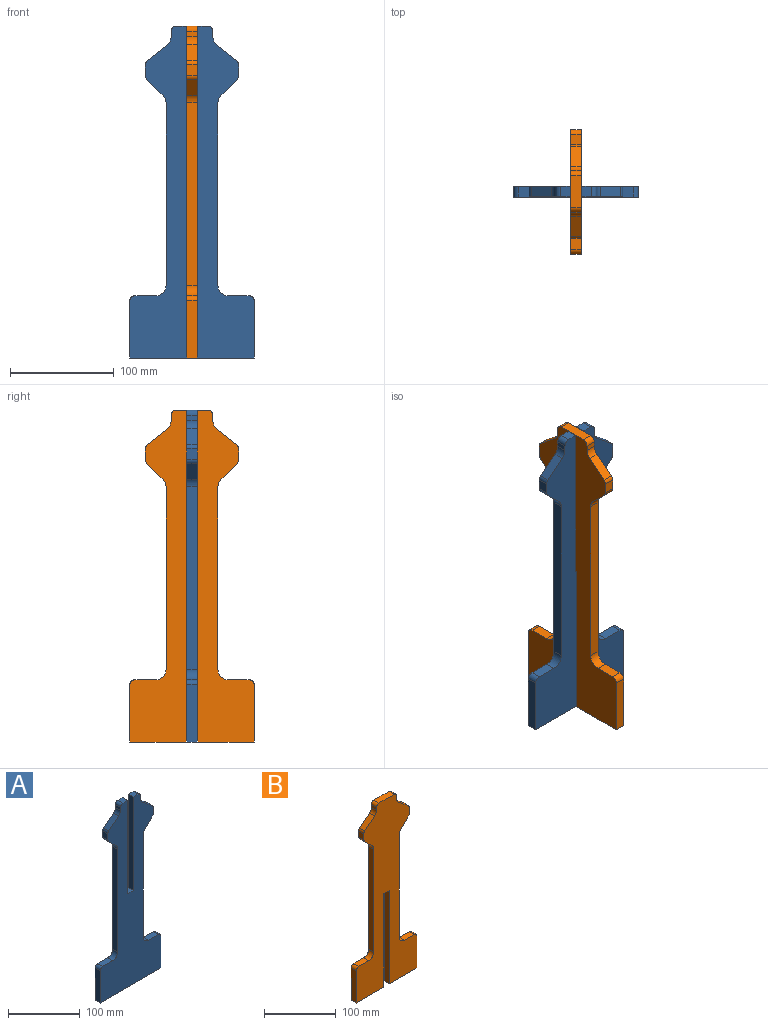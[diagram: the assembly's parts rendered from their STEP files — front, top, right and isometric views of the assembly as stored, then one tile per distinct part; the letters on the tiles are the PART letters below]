
ASSEMBLY  parts=2 mates=1
PART A: 36 faces, bbox 120x10x320 mm
  f0: plane 120x10mm, normal (0,0,-1), area 1200mm2, adj f1,f33,f34,f35
  f1: plane 55x10mm, normal (1,0,0), area 550mm2, adj f0,f2,f34,f35
  f2: cylinder r=5mm len=10mm, axis (0,-1,0), area 78.5mm2, adj f1,f3,f34,f35
  f3: plane 20x10mm, normal (0,0,1), area 200mm2, adj f2,f4,f34,f35
  f4: cylinder r=10mm len=10mm, axis (0,-1,0), area 157.1mm2, adj f3,f5,f34,f35
  f5: plane 175.86x10mm, normal (1,0,0), area 1758.6mm2, adj f4,f6,f34,f35
  f6: cylinder r=10mm len=10mm, axis (0,-1,0), area 78.5mm2, adj f5,f7,f34,f35
  f7: plane 15.61x15.61mm, normal (0.71,0,-0.71), area 220.7mm2, adj f6,f8,f34,f35
  f8: cylinder r=5mm len=10mm, axis (0,-1,0), area 39.3mm2, adj f7,f9,f34,f35
  f9: plane 10.53x10mm, normal (1,0,0), area 105.3mm2, adj f8,f10,f34,f35
  f10: cylinder r=5mm len=10mm, axis (0,-1,0), area 44.8mm2, adj f9,f11,f34,f35
  f11: plane 19.37x15.5mm, normal (0.62,0,0.78), area 248.1mm2, adj f10,f12,f34,f35
  f12: cylinder r=10mm len=10mm, axis (0,-1,0), area 89.6mm2, adj f11,f13,f34,f35
  f13: plane 10x5.19mm, normal (1,0,0), area 51.9mm2, adj f12,f14,f34,f35
  f14: cylinder r=5mm len=10mm, axis (0,-1,0), area 78.5mm2, adj f13,f15,f34,f35
  f15: plane 10x9.5mm, normal (0,0,1), area 95mm2, adj f14,f16,f34,f35
  f16: plane 160x10mm, normal (-1,0,0), area 1600mm2, adj f15,f17,f34,f35
  f17: plane 11x10mm, normal (0,0,1), area 110mm2, adj f16,f18,f34,f35
  f18: plane 160x10mm, normal (1,0,0), area 1600mm2, adj f17,f19,f34,f35
  f19: plane 10x9.5mm, normal (0,0,1), area 95mm2, adj f18,f20,f34,f35
  f20: cylinder r=5mm len=10mm, axis (0,-1,0), area 78.5mm2, adj f19,f21,f34,f35
  f21: plane 10x5.19mm, normal (-1,0,0), area 51.9mm2, adj f20,f22,f34,f35
  f22: cylinder r=10mm len=10mm, axis (0,-1,0), area 89.6mm2, adj f21,f23,f34,f35
  f23: plane 19.37x15.5mm, normal (-0.62,0,0.78), area 248.1mm2, adj f22,f24,f34,f35
  f24: cylinder r=5mm len=10mm, axis (0,-1,0), area 44.8mm2, adj f23,f25,f34,f35
  f25: plane 10.53x10mm, normal (-1,0,0), area 105.3mm2, adj f24,f26,f34,f35
  f26: cylinder r=5mm len=10mm, axis (0,-1,0), area 39.3mm2, adj f25,f27,f34,f35
  f27: plane 15.61x15.61mm, normal (-0.71,0,-0.71), area 220.7mm2, adj f26,f28,f34,f35
  f28: cylinder r=10mm len=10mm, axis (0,-1,0), area 78.5mm2, adj f27,f29,f34,f35
  f29: plane 175.86x10mm, normal (-1,0,0), area 1758.6mm2, adj f28,f30,f34,f35
  f30: cylinder r=10mm len=10mm, axis (0,-1,0), area 157.1mm2, adj f29,f31,f34,f35
  f31: plane 20x10mm, normal (0,0,1), area 200mm2, adj f30,f32,f34,f35
  f32: cylinder r=5mm len=10mm, axis (0,-1,0), area 78.5mm2, adj f31,f33,f34,f35
  f33: plane 55x10mm, normal (-1,0,0), area 550mm2, adj f0,f32,f34,f35
  f34: plane 320x120mm, normal (0,1,0), area 19619.6mm2, adj f0,f1,f2,f3,f4,f5,f6,f7
  f35: plane 320x120mm, normal (0,-1,0), area 19619.6mm2, adj f0,f1,f2,f3,f4,f5,f6,f7
PART B: 36 faces, bbox 120x10x320 mm
  f0: plane 160x10mm, normal (1,0,0), area 1600mm2, adj f1,f33,f34,f35
  f1: plane 11x10mm, normal (0,0,-1), area 110mm2, adj f0,f2,f34,f35
  f2: plane 160x10mm, normal (-1,0,0), area 1600mm2, adj f1,f3,f34,f35
  f3: plane 54.5x10mm, normal (0,0,-1), area 545mm2, adj f2,f4,f34,f35
  f4: plane 55x10mm, normal (1,0,0), area 550mm2, adj f3,f5,f34,f35
  f5: cylinder r=5mm len=10mm, axis (0,1,0), area 78.5mm2, adj f4,f6,f34,f35
  f6: plane 20x10mm, normal (0,0,1), area 200mm2, adj f5,f7,f34,f35
  f7: cylinder r=10mm len=10mm, axis (0,1,0), area 157.1mm2, adj f6,f8,f34,f35
  f8: plane 175.86x10mm, normal (1,0,0), area 1758.6mm2, adj f7,f9,f34,f35
  f9: cylinder r=10mm len=10mm, axis (0,1,0), area 78.5mm2, adj f8,f10,f34,f35
  f10: plane 15.61x15.61mm, normal (0.71,0,-0.71), area 220.7mm2, adj f9,f11,f34,f35
  f11: cylinder r=5mm len=10mm, axis (0,1,0), area 39.3mm2, adj f10,f12,f34,f35
  f12: plane 10.53x10mm, normal (1,0,0), area 105.3mm2, adj f11,f13,f34,f35
  f13: cylinder r=5mm len=10mm, axis (0,1,0), area 44.8mm2, adj f12,f14,f34,f35
  f14: plane 19.37x15.5mm, normal (0.62,0,0.78), area 248.1mm2, adj f13,f15,f34,f35
  f15: cylinder r=10mm len=10mm, axis (0,1,0), area 89.6mm2, adj f14,f16,f34,f35
  f16: plane 10x5.19mm, normal (1,0,0), area 51.9mm2, adj f15,f17,f34,f35
  f17: cylinder r=5mm len=10mm, axis (0,1,0), area 78.5mm2, adj f16,f18,f34,f35
  f18: plane 30x10mm, normal (0,0,1), area 300mm2, adj f17,f19,f34,f35
  f19: cylinder r=5mm len=10mm, axis (0,1,0), area 78.5mm2, adj f18,f20,f34,f35
  f20: plane 10x5.19mm, normal (-1,0,0), area 51.9mm2, adj f19,f21,f34,f35
  f21: cylinder r=10mm len=10mm, axis (0,1,0), area 89.6mm2, adj f20,f22,f34,f35
  f22: plane 19.37x15.5mm, normal (-0.62,0,0.78), area 248.1mm2, adj f21,f23,f34,f35
  f23: cylinder r=5mm len=10mm, axis (0,1,0), area 44.8mm2, adj f22,f24,f34,f35
  f24: plane 10.53x10mm, normal (-1,0,0), area 105.3mm2, adj f23,f25,f34,f35
  f25: cylinder r=5mm len=10mm, axis (0,1,0), area 39.3mm2, adj f24,f26,f34,f35
  f26: plane 15.61x15.61mm, normal (-0.71,0,-0.71), area 220.7mm2, adj f25,f27,f34,f35
  f27: cylinder r=10mm len=10mm, axis (0,1,0), area 78.5mm2, adj f26,f28,f34,f35
  f28: plane 175.86x10mm, normal (-1,0,0), area 1758.6mm2, adj f27,f29,f34,f35
  f29: cylinder r=10mm len=10mm, axis (0,1,0), area 157.1mm2, adj f28,f30,f34,f35
  f30: plane 20x10mm, normal (0,0,1), area 200mm2, adj f29,f31,f34,f35
  f31: cylinder r=5mm len=10mm, axis (0,1,0), area 78.5mm2, adj f30,f32,f34,f35
  f32: plane 55x10mm, normal (-1,0,0), area 550mm2, adj f31,f33,f34,f35
  f33: plane 54.5x10mm, normal (0,0,-1), area 545mm2, adj f0,f32,f34,f35
  f34: plane 320x120mm, normal (0,-1,0), area 19619.6mm2, adj f0,f1,f2,f3,f4,f5,f6,f7
  f35: plane 320x120mm, normal (0,1,0), area 19619.6mm2, adj f0,f1,f2,f3,f4,f5,f6,f7
PLACE A at identity
PLACE B rot(axis=(0,0,1),90deg) t=(-5,5,0)mm
MATE fastened B.f1 <-> A.f17  axis (0,0,-1) through (0,5,130)mm
